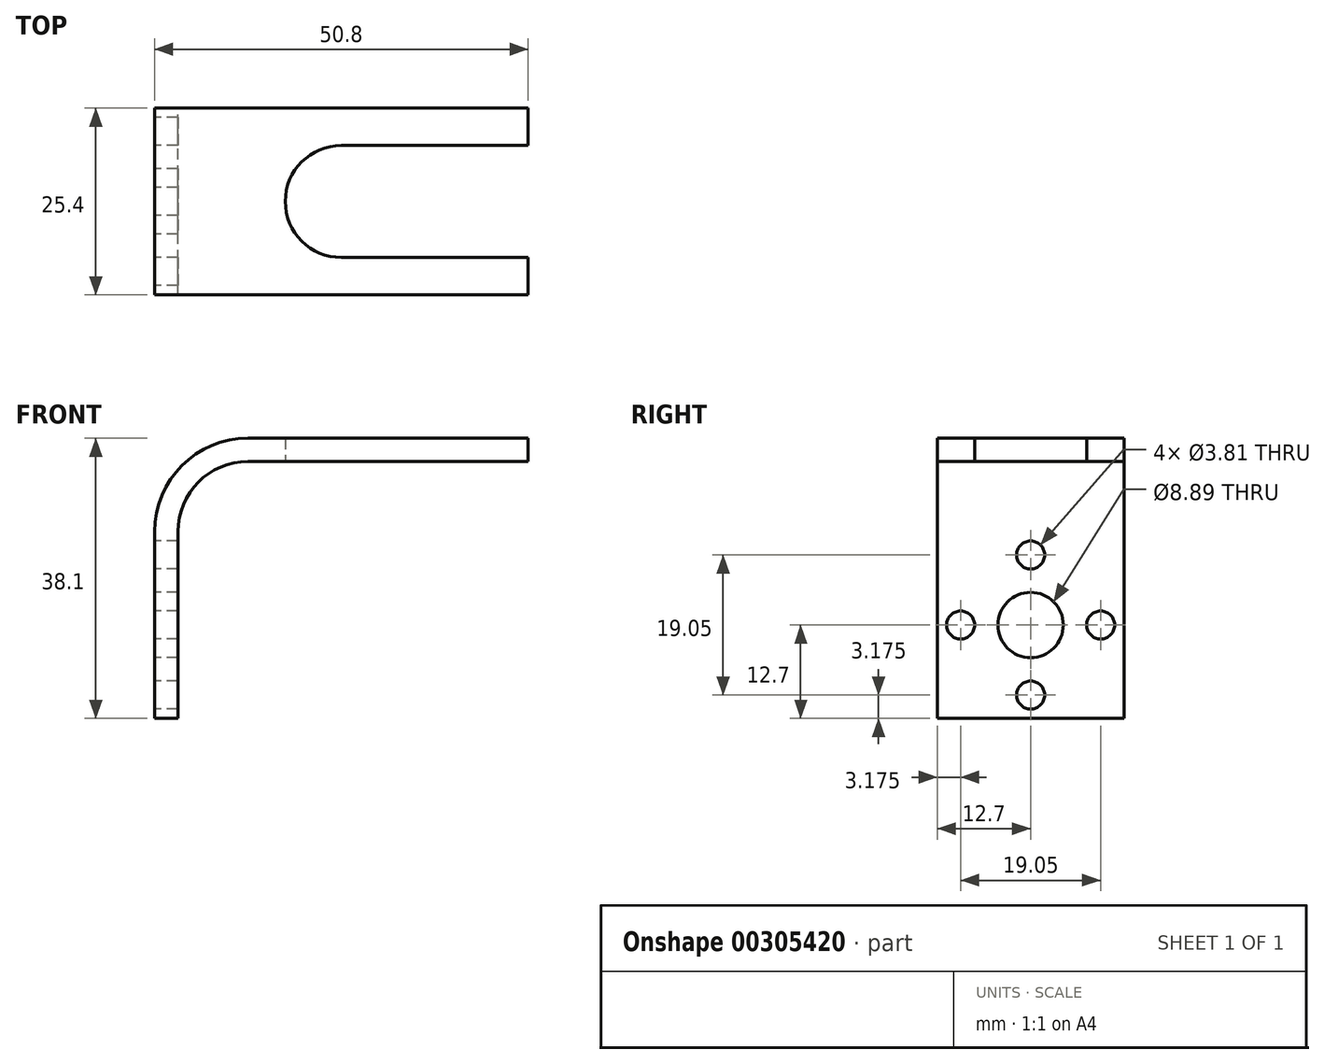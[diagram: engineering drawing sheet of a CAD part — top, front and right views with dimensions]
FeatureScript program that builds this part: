
annotation { "Feature Type Name" : "Feature", "Feature Type Description" : "" }
export const myFeature = defineFeature(function(context is Context, id is Id, definition is map)
    precondition{}
    {
        {
            var Q0;
            Q0=qCreatedBy(makeId("Front.planeOp"),FACE);
            var sketch = newSketch(context, id + "F0", { "sketchPlane" : qUnion([Q0])});
            skLineSegment(sketch, "E0", {"start": v(0, 0) * mm, "end": v(0, 25.4) * mm});
            skLineSegment(sketch, "E1", {"start": v(12.7, 38.1) * mm, "end": v(50.8, 38.1) * mm});
            skPoint(sketch, "E2.visualSharp", {"position": v(0, 38.1) * mm});
            skArc(sketch, "E2.filletArc", {"start": v(12.7, 38.1) * mm, "mid": v(3.72, 34.38) * mm, "end": v(0, 25.4) * mm});
            skLineSegment(sketch, "E3.0", {"start": v(12.7, 34.93) * mm, "end": v(50.8, 34.93) * mm});
            skArc(sketch, "E3.1", {"start": v(12.7, 34.93) * mm, "mid": v(5.96, 32.14) * mm, "end": v(3.17, 25.4) * mm});
            skLineSegment(sketch, "E3.2", {"start": v(3.17, 0) * mm, "end": v(3.17, 25.4) * mm});
            skLineSegment(sketch, "E4", {"start": v(50.8, 34.93) * mm, "end": v(50.8, 38.1) * mm});
            skLineSegment(sketch, "E5", {"start": v(0, 0) * mm, "end": v(3.17, 0) * mm});
            skLineSegment(sketch, "E6", {"start": v(3.17, 0) * mm, "end": v(0, 0) * mm});
            skSolve(sketch);
        }
        {
            var Q0;
            Q0 = qSketchRegion(id + "F0", true);
            extrude(context, id + "F1", {"entities" : qUnion([Q0]), "depth" : 25.4 * mm});
        }
        {
            var Q0;
            Q0=makeQuery(id+"F1.opExtrude","SWEPT_FACE",FACE,{"disambiguationData":[OSD([sQuery(id+"F0.wireOp",EDGE,"E3.0")])]});
            var sketch = newSketch(context, id + "F2", { "sketchPlane" : qUnion([Q0])});
            skLineSegment(sketch, "E7", {"start": v(56.9, 12.7) * mm, "end": v(-12.24, 12.7) * mm, "construction": true});
            skPoint(sketch, "E7.startSnap0", {"position": v(50.8, 12.7) * mm});
            skLineSegment(sketch, "E8", {"start": v(50.8, 20.32) * mm, "end": v(25.4, 20.32) * mm});
            skArc(sketch, "E9", {"start": v(25.4, 20.32) * mm, "mid": v(20.01, 18.09) * mm, "end": v(17.78, 12.7) * mm});
            skLineSegment(sketch, "E10.MirrorCS", {"start": v(50.8, 5.08) * mm, "end": v(25.4, 5.08) * mm});
            skArc(sketch, "E11.MirrorCS", {"start": v(25.4, 5.08) * mm, "mid": v(20.01, 7.31) * mm, "end": v(17.78, 12.7) * mm});
            skLineSegment(sketch, "E12", {"start": v(50.8, 5.08) * mm, "end": v(50.8, 20.32) * mm});
            skSolve(sketch);
        }
        {
            var Q0;
            Q0 = qSketchRegion(id + "F2", true);
            extrude(context, id + "F3", {"entities" : qUnion([Q0]), "operationType" : NewBodyOperationType.REMOVE, "endBound" : BoundingType.UP_TO_NEXT, "oppositeDirection" : true, "depth" : 25.4 * mm});
        }
        {
            var Q0;
            Q0=makeQuery(id+"F1.opExtrude","SWEPT_FACE",FACE,{"disambiguationData":[OSD([sQuery(id+"F0.wireOp",EDGE,"E0")])]});
            var sketch = newSketch(context, id + "F4", { "sketchPlane" : qUnion([Q0])});
            skCircle(sketch, "E13", {"center": v(12.7, 12.7) * mm, "radius": 4.45 * mm});
            skPoint(sketch, "E13.centerSnap0", {"position": v(12.7, 0) * mm});
            skCircle(sketch, "E14", {"center": v(22.23, 12.7) * mm, "radius": 1.9 * mm});
            skPoint(sketch, "E14.centerSnap0", {"position": v(25.4, 12.7) * mm});
            skCircle(sketch, "E15", {"center": v(12.7, 3.18) * mm, "radius": 1.9 * mm});
            skCircle(sketch, "E16", {"center": v(3.18, 12.7) * mm, "radius": 1.9 * mm});
            skPoint(sketch, "E16.centerSnap0", {"position": v(0, 12.7) * mm});
            skCircle(sketch, "E17", {"center": v(12.7, 22.23) * mm, "radius": 1.9 * mm});
            skLineSegment(sketch, "E18", {"start": v(12.7, -4.19) * mm, "end": v(12.7, 50.75) * mm, "construction": true});
            skLineSegment(sketch, "E19", {"start": v(-6.22, 12.7) * mm, "end": v(39.3, 12.7) * mm, "construction": true});
            skCircle(sketch, "E20", {"center": v(12.7, 12.7) * mm, "radius": 9.53 * mm, "construction": true});
            skSolve(sketch);
        }
        {
            var Q0;
            Q0 = qSketchRegion(id + "F4", true);
            extrude(context, id + "F5", {"entities" : qUnion([Q0]), "operationType" : NewBodyOperationType.REMOVE, "endBound" : BoundingType.UP_TO_NEXT, "oppositeDirection" : true, "depth" : 25.4 * mm});
        }
    });
